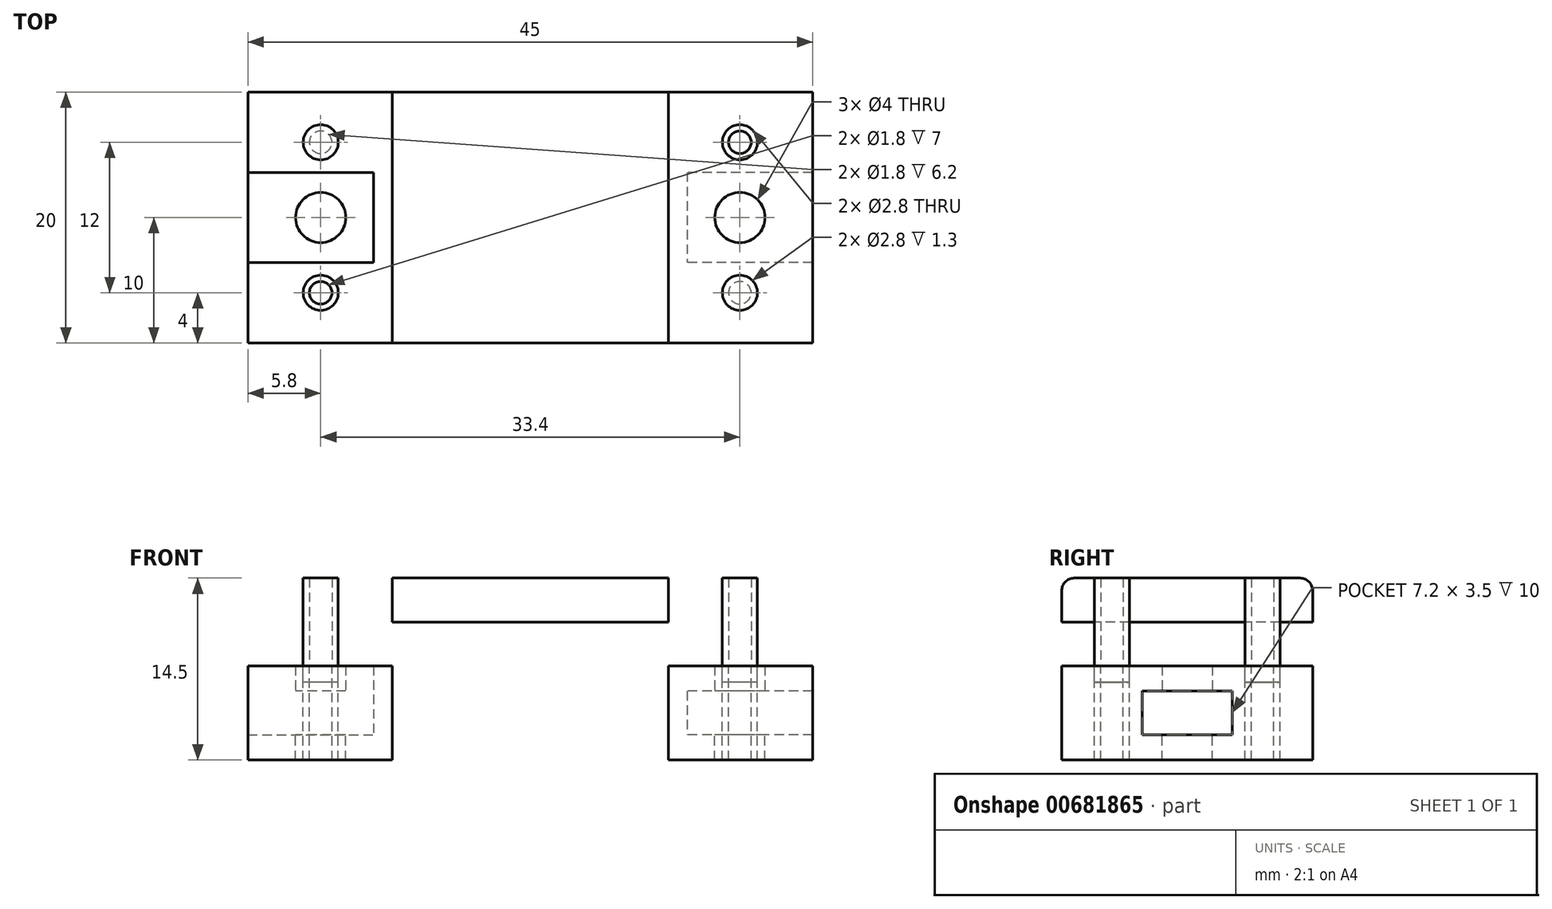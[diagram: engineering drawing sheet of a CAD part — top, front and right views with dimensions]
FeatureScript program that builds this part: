
annotation { "Feature Type Name" : "Feature", "Feature Type Description" : "" }
export const myFeature = defineFeature(function(context is Context, id is Id, definition is map)
    precondition{}
    {
        {
            var Q0;
            Q0=qCreatedBy(makeId("Top.planeOp"),FACE);
            var sketch = newSketch(context, id + "F0", { "sketchPlane" : qUnion([Q0])});
            skLineSegment(sketch, "E0.bottom", {"start": v(22.5, 10) * mm, "end": v(-22.5, 10) * mm});
            skLineSegment(sketch, "E0.top", {"start": v(22.5, -10) * mm, "end": v(-22.5, -10) * mm});
            skLineSegment(sketch, "E0.left", {"start": v(22.5, 10) * mm, "end": v(22.5, -10) * mm});
            skLineSegment(sketch, "E0.right", {"start": v(-22.5, 10) * mm, "end": v(-22.5, -10) * mm});
            skPoint(sketch, "E0.middle", {"position": v(0, 0) * mm});
            skLineSegment(sketch, "E1.bottom", {"start": v(-22.5, 3.6) * mm, "end": v(-12.5, 3.6) * mm});
            skLineSegment(sketch, "E1.top", {"start": v(-22.5, -3.6) * mm, "end": v(-12.5, -3.6) * mm});
            skLineSegment(sketch, "E1.left", {"start": v(-22.5, 3.6) * mm, "end": v(-22.5, -3.6) * mm});
            skLineSegment(sketch, "E1.right", {"start": v(-12.5, 3.6) * mm, "end": v(-12.5, -3.6) * mm});
            skPoint(sketch, "E2", {"position": v(-22.5, 0) * mm});
            skLineSegment(sketch, "E3.MirrorCS", {"start": v(22.5, 3.6) * mm, "end": v(12.5, 3.6) * mm});
            skLineSegment(sketch, "E4.MirrorCS", {"start": v(12.5, 3.6) * mm, "end": v(12.5, -3.6) * mm});
            skLineSegment(sketch, "E5.MirrorCS", {"start": v(22.5, -3.6) * mm, "end": v(12.5, -3.6) * mm});
            skLineSegment(sketch, "E6", {"start": v(12.5, 0) * mm, "end": v(14.7, 0) * mm, "construction": true});
            skCircle(sketch, "E7", {"center": v(16.7, 0) * mm, "radius": 2 * mm});
            skPoint(sketch, "E8", {"position": v(18.7, 0) * mm});
            skPoint(sketch, "E9", {"position": v(14.7, 0) * mm});
            skCircle(sketch, "E10.MirrorC", {"center": v(-16.7, 0) * mm, "radius": 2 * mm});
            skSolve(sketch);
        }
        {
            var Q0;
            {var subQ1=sQuery(id+"F0.wireOp",EDGE,"E0.bottom");Q0=makeQuery(id+"F0.imprint","IMPRINT",FACE,{"disambiguationData":[TD([[makeQuery(id+"F0.imprint","IMPRINT",EDGE,{"derivedFrom":subQ1}),1.0]])]});}
            var Q1;
            Q1=makeQuery(id+"F0.imprint","IMPRINT",FACE,{"disambiguationData":[TD([[makeQuery(id+"F0.imprint","IMPRINT",EDGE,{"derivedFrom":sQuery(id+"F0.wireOp",EDGE,"E1.bottom")}),-1.0]])]});
            var Q2;
            {var subQ0=sQuery(id+"F0.wireOp",EDGE,"E3.MirrorCS");Q2=makeQuery(id+"F0.imprint","IMPRINT",FACE,{"disambiguationData":[TD([[makeQuery(id+"F0.imprint","IMPRINT",EDGE,{"derivedFrom":subQ0}),1.0]])]});}
            extrude(context, id + "F1", {"entities" : qUnion([Q0, Q1, Q2]), "oppositeDirection" : true, "depth" : 2 * mm, "offsetDistance" : 25 * mm});
        }
        {
            var Q0;
            {var subQ5=sQuery(id+"F0.wireOp",EDGE,"E0.bottom");Q0=makeQuery(id+"F0.imprint","IMPRINT",FACE,{"disambiguationData":[TD([[makeQuery(id+"F0.imprint","IMPRINT",EDGE,{"derivedFrom":subQ5}),1.0]])]});}
            extrude(context, id + "F2", {"entities" : qUnion([Q0]), "operationType" : NewBodyOperationType.ADD, "depth" : 3.5 * mm, "offsetDistance" : 25 * mm});
        }
        {
            var Q0;
            Q0=makeQuery(id+"F2.opExtrude","CAP_FACE",FACE,{"disambiguationData":[OSD([sQuery(id+"F0.wireOp",EDGE,"E0.bottom"),sQuery(id+"F0.wireOp",EDGE,"E0.top"),sQuery(id+"F0.wireOp",EDGE,"E0.left"),sQuery(id+"F0.wireOp",EDGE,"E0.right"),sQuery(id+"F0.wireOp",EDGE,"E1.bottom"),sQuery(id+"F0.wireOp",EDGE,"E1.top"),sQuery(id+"F0.wireOp",EDGE,"E1.right"),sQuery(id+"F0.wireOp",EDGE,"E3.MirrorCS"),sQuery(id+"F0.wireOp",EDGE,"E4.MirrorCS"),sQuery(id+"F0.wireOp",EDGE,"E5.MirrorCS")])],"isStart":false});
            var sketch = newSketch(context, id + "F3", { "sketchPlane" : qUnion([Q0])});
            skLineSegment(sketch, "E11.bottom", {"start": v(-22.5, 10) * mm, "end": v(22.5, 10) * mm});
            skLineSegment(sketch, "E11.top", {"start": v(-22.5, -10) * mm, "end": v(22.5, -10) * mm});
            skLineSegment(sketch, "E11.left", {"start": v(-22.5, 10) * mm, "end": v(-22.5, -10) * mm});
            skLineSegment(sketch, "E11.right", {"start": v(22.5, 10) * mm, "end": v(22.5, -10) * mm});
            skSolve(sketch);
        }
        {
            var Q0;
            Q0 = qSketchRegion(id + "F3", true);
            extrude(context, id + "F4", {"entities" : qUnion([Q0]), "operationType" : NewBodyOperationType.ADD, "depth" : 2 * mm, "offsetDistance" : 25 * mm});
        }
        {
            var Q0;
            Q0=makeQuery(id+"F0.imprint","IMPRINT",FACE,{"disambiguationData":[TD([[makeQuery(id+"F0.imprint","IMPRINT",EDGE,{"derivedFrom":sQuery(id+"F0.wireOp",EDGE,"E7")}),1.0]])]});
            var Q1;
            Q1=makeQuery(id+"F0.imprint","IMPRINT",FACE,{"disambiguationData":[TD([[makeQuery(id+"F0.imprint","IMPRINT",EDGE,{"derivedFrom":sQuery(id+"F0.wireOp",EDGE,"E10.MirrorC")}),-1.0]])]});
            extrude(context, id + "F5", {"entities" : qUnion([Q0, Q1]), "operationType" : NewBodyOperationType.REMOVE, "depth" : 25 * mm, "offsetDistance" : 25 * mm});
        }
        {
            var Q0;
            Q0=makeQuery(id+"F4.opExtrude","CAP_FACE",FACE,{"disambiguationData":[OSD([sQuery(id+"F3.wireOp",EDGE,"E11.bottom"),sQuery(id+"F3.wireOp",EDGE,"E11.top"),sQuery(id+"F3.wireOp",EDGE,"E11.left"),sQuery(id+"F3.wireOp",EDGE,"E11.right")])],"isStart":false});
            var sketch = newSketch(context, id + "F6", { "sketchPlane" : qUnion([Q0])});
            skLineSegment(sketch, "E12.bottom", {"start": v(11, 10) * mm, "end": v(-11, 10) * mm});
            skLineSegment(sketch, "E12.top", {"start": v(11, -10) * mm, "end": v(-11, -10) * mm});
            skLineSegment(sketch, "E12.left", {"start": v(11, 10) * mm, "end": v(11, -10) * mm});
            skLineSegment(sketch, "E12.right", {"start": v(-11, 10) * mm, "end": v(-11, -10) * mm});
            skPoint(sketch, "E12.middle", {"position": v(0, 0) * mm});
            skLineSegment(sketch, "E13", {"start": v(-16.7, 10) * mm, "end": v(-16.7, 2) * mm, "construction": true});
            skPoint(sketch, "E14", {"position": v(-16.7, 6) * mm});
            skCircle(sketch, "E15", {"center": v(-16.7, 6) * mm, "radius": 0.9 * mm});
            skCircle(sketch, "E16", {"center": v(-16.7, 6) * mm, "radius": 1.4 * mm});
            skCircle(sketch, "E17.MirrorC", {"center": v(16.7, 6) * mm, "radius": 1.4 * mm});
            skCircle(sketch, "E18.MirrorC", {"center": v(16.7, 6) * mm, "radius": 0.9 * mm});
            skCircle(sketch, "E19.MirrorC", {"center": v(-16.7, -6) * mm, "radius": 1.4 * mm});
            skCircle(sketch, "E20.MirrorC", {"center": v(-16.7, -6) * mm, "radius": 0.9 * mm});
            skCircle(sketch, "E21.MirrorC", {"center": v(16.7, -6) * mm, "radius": 1.4 * mm});
            skCircle(sketch, "E22.MirrorC", {"center": v(16.7, -6) * mm, "radius": 0.9 * mm});
            skSolve(sketch);
        }
        {
            var Q0;
            Q0=makeQuery(id+"F6.imprint","IMPRINT",FACE,{"disambiguationData":[TD([[makeQuery(id+"F6.imprint","IMPRINT",EDGE,{"derivedFrom":sQuery(id+"F6.wireOp",EDGE,"E12.bottom")}),1.0]])]});
            var Q1;
            Q1=makeQuery(id+"F6.imprint","IMPRINT",FACE,{"disambiguationData":[TD([[makeQuery(id+"F6.imprint","IMPRINT",EDGE,{"derivedFrom":sQuery(id+"F6.wireOp",EDGE,"E15")}),1.0]])]});
            var Q2;
            Q2=makeQuery(id+"F6.imprint","IMPRINT",FACE,{"disambiguationData":[TD([[makeQuery(id+"F6.imprint","IMPRINT",EDGE,{"derivedFrom":sQuery(id+"F6.wireOp",EDGE,"E18.MirrorC")}),-1.0]])]});
            var Q3;
            Q3=makeQuery(id+"F6.imprint","IMPRINT",FACE,{"disambiguationData":[TD([[makeQuery(id+"F6.imprint","IMPRINT",EDGE,{"derivedFrom":sQuery(id+"F6.wireOp",EDGE,"E22.MirrorC")}),1.0]])]});
            var Q4;
            Q4=makeQuery(id+"F6.imprint","IMPRINT",FACE,{"disambiguationData":[TD([[makeQuery(id+"F6.imprint","IMPRINT",EDGE,{"derivedFrom":sQuery(id+"F6.wireOp",EDGE,"E20.MirrorC")}),-1.0]])]});
            var Q5;
            {var subQ0=sQuery(id+"F0.wireOp",EDGE,"E0.right");var subQ1=sQuery(id+"F0.wireOp",EDGE,"E0.top");var subQ2=sQuery(id+"F0.wireOp",EDGE,"E1.left");var subQ4=sQuery(id+"F0.wireOp",EDGE,"E0.bottom");var subQ6=sQuery(id+"F0.wireOp",EDGE,"E10.MirrorC");Q5=makeQuery(id+"F2.boolean.opBoolean","SPLIT",FACE,{"disambiguationData":[TD([makeQuery(id+"F1.opExtrude","SWEPT_FACE",FACE,{"disambiguationData":[OSD([subQ6])]})])],"derivedFrom":makeQuery(id+"F1.opExtrude","CAP_FACE",FACE,{"disambiguationData":[OSD([subQ4,subQ1,sQuery(id+"F0.wireOp",EDGE,"E0.left"),subQ0,subQ2,sQuery(id+"F0.wireOp",EDGE,"E7"),subQ6])],"isStart":true})});}
            extrude(context, id + "F7", {"entities" : qUnion([Q0, Q1, Q2, Q3, Q4]), "operationType" : NewBodyOperationType.REMOVE, "oppositeDirection" : true, "depth" : 25 * mm, "endBoundEntityFace" : qUnion([Q5]), "offsetDistance" : 25 * mm});
        }
        {
            var Q0;
            Q0=makeQuery(id+"F6.imprint","IMPRINT",FACE,{"disambiguationData":[TD([[makeQuery(id+"F6.imprint","IMPRINT",EDGE,{"derivedFrom":sQuery(id+"F6.wireOp",EDGE,"E15")}),-1.0]])]});
            var Q1;
            Q1=makeQuery(id+"F6.imprint","IMPRINT",FACE,{"disambiguationData":[TD([[makeQuery(id+"F6.imprint","IMPRINT",EDGE,{"derivedFrom":sQuery(id+"F6.wireOp",EDGE,"E19.MirrorC")}),-1.0]])]});
            var Q2;
            Q2=makeQuery(id+"F6.imprint","IMPRINT",FACE,{"disambiguationData":[TD([[makeQuery(id+"F6.imprint","IMPRINT",EDGE,{"derivedFrom":sQuery(id+"F6.wireOp",EDGE,"E21.MirrorC")}),1.0]])]});
            var Q3;
            Q3=makeQuery(id+"F6.imprint","IMPRINT",FACE,{"disambiguationData":[TD([[makeQuery(id+"F6.imprint","IMPRINT",EDGE,{"derivedFrom":sQuery(id+"F6.wireOp",EDGE,"E17.MirrorC")}),-1.0]])]});
            extrude(context, id + "F8", {"entities" : qUnion([Q0, Q1, Q2, Q3]), "operationType" : NewBodyOperationType.REMOVE, "oppositeDirection" : true, "depth" : 1.3 * mm, "offsetDistance" : 25 * mm});
        }
        {
            var Q0;
            {var subQ4=sQuery(id+"F6.wireOp",EDGE,"E12.right");Q0=makeQuery(id+"F6.imprint","IMPRINT",FACE,{"disambiguationData":[TD([[makeQuery(id+"F6.imprint","IMPRINT",EDGE,{"derivedFrom":subQ4}),-1.0]])]});}
            var Q1;
            Q1=makeQuery(id+"F6.imprint","IMPRINT",FACE,{"disambiguationData":[TD([[makeQuery(id+"F6.imprint","IMPRINT",EDGE,{"derivedFrom":sQuery(id+"F6.wireOp",EDGE,"E12.bottom")}),1.0]])]});
            var Q2;
            {var subQ2=sQuery(id+"F6.wireOp",EDGE,"E12.left");Q2=makeQuery(id+"F6.imprint","IMPRINT",FACE,{"disambiguationData":[TD([[makeQuery(id+"F6.imprint","IMPRINT",EDGE,{"derivedFrom":subQ2}),1.0]])]});}
            var Q3;
            Q3=makeQuery(id+"F6.imprint","IMPRINT",FACE,{"disambiguationData":[TD([[makeQuery(id+"F6.imprint","IMPRINT",EDGE,{"derivedFrom":sQuery(id+"F6.wireOp",EDGE,"E17.MirrorC")}),-1.0]])]});
            var Q4;
            Q4=makeQuery(id+"F6.imprint","IMPRINT",FACE,{"disambiguationData":[TD([[makeQuery(id+"F6.imprint","IMPRINT",EDGE,{"derivedFrom":sQuery(id+"F6.wireOp",EDGE,"E18.MirrorC")}),-1.0]])]});
            var Q5;
            Q5=makeQuery(id+"F6.imprint","IMPRINT",FACE,{"disambiguationData":[TD([[makeQuery(id+"F6.imprint","IMPRINT",EDGE,{"derivedFrom":sQuery(id+"F6.wireOp",EDGE,"E21.MirrorC")}),1.0]])]});
            var Q6;
            Q6=makeQuery(id+"F6.imprint","IMPRINT",FACE,{"disambiguationData":[TD([[makeQuery(id+"F6.imprint","IMPRINT",EDGE,{"derivedFrom":sQuery(id+"F6.wireOp",EDGE,"E22.MirrorC")}),1.0]])]});
            var Q7;
            Q7=makeQuery(id+"F6.imprint","IMPRINT",FACE,{"disambiguationData":[TD([[makeQuery(id+"F6.imprint","IMPRINT",EDGE,{"derivedFrom":sQuery(id+"F6.wireOp",EDGE,"E20.MirrorC")}),-1.0]])]});
            var Q8;
            Q8=makeQuery(id+"F6.imprint","IMPRINT",FACE,{"disambiguationData":[TD([[makeQuery(id+"F6.imprint","IMPRINT",EDGE,{"derivedFrom":sQuery(id+"F6.wireOp",EDGE,"E19.MirrorC")}),-1.0]])]});
            var Q9;
            Q9=makeQuery(id+"F6.imprint","IMPRINT",FACE,{"disambiguationData":[TD([[makeQuery(id+"F6.imprint","IMPRINT",EDGE,{"derivedFrom":sQuery(id+"F6.wireOp",EDGE,"E15")}),-1.0]])]});
            var Q10;
            Q10=makeQuery(id+"F6.imprint","IMPRINT",FACE,{"disambiguationData":[TD([[makeQuery(id+"F6.imprint","IMPRINT",EDGE,{"derivedFrom":sQuery(id+"F6.wireOp",EDGE,"E15")}),1.0]])]});
            extrude(context, id + "F9", {"entities" : qUnion([Q0, Q1, Q2, Q3, Q4, Q5, Q6, Q7, Q8, Q9, Q10]), "depth" : 7 * mm, "offsetDistance" : 25 * mm});
        }
        {
            var Q0;
            Q0=makeQuery(id+"F9.opExtrude","CAP_FACE",FACE,{"disambiguationData":[OSD([sQuery(id+"F0.wireOp",EDGE,"E7"),sQuery(id+"F0.wireOp",EDGE,"E10.MirrorC"),sQuery(id+"F3.wireOp",EDGE,"E11.bottom"),sQuery(id+"F3.wireOp",EDGE,"E11.top"),sQuery(id+"F3.wireOp",EDGE,"E11.left"),sQuery(id+"F3.wireOp",EDGE,"E11.right"),sQuery(id+"F6.wireOp",EDGE,"E12.bottom"),sQuery(id+"F6.wireOp",EDGE,"E12.top")])],"isStart":false});
            var sketch = newSketch(context, id + "F10", { "sketchPlane" : qUnion([Q0])});
            skCircle(sketch, "E23.0", {"center": v(-16.7, 0) * mm, "radius": 3.6 * mm});
            skLineSegment(sketch, "E24", {"start": v(-16.7, 2) * mm, "end": v(-16.7, -2) * mm, "construction": true});
            skCircle(sketch, "E25.MirrorC", {"center": v(16.7, 0) * mm, "radius": 3.6 * mm});
            skSolve(sketch);
        }
        {
            var Q0;
            Q0=makeQuery(id+"F10.imprint","IMPRINT",FACE,{"disambiguationData":[TD([[makeQuery(id+"F10.imprint","IMPRINT",EDGE,{"derivedFrom":sQuery(id+"F10.wireOp",EDGE,"E23.0")}),1.0]])]});
            var Q1;
            Q1=makeQuery(id+"F10.imprint","IMPRINT",FACE,{"disambiguationData":[TD([[makeQuery(id+"F10.imprint","IMPRINT",EDGE,{"derivedFrom":sQuery(id+"F10.wireOp",EDGE,"E25.MirrorC")}),-1.0]])]});
            extrude(context, id + "F11", {"entities" : qUnion([Q0, Q1]), "operationType" : NewBodyOperationType.REMOVE, "oppositeDirection" : true, "depth" : 2.5 * mm, "offsetDistance" : 25 * mm});
        }
        {
            var Q0;
            Q0=makeQuery(id+"F9.opExtrude","CAP_EDGE",EDGE,{"disambiguationData":[OSD([sQuery(id+"F3.wireOp",EDGE,"E11.top"),sQuery(id+"F6.wireOp",EDGE,"E12.top")])],"isStart":false});
            var Q1;
            Q1=makeQuery(id+"F9.opExtrude","CAP_EDGE",EDGE,{"disambiguationData":[OSD([sQuery(id+"F3.wireOp",EDGE,"E11.right")])],"isStart":false});
            var Q2;
            Q2=makeQuery(id+"F9.opExtrude","CAP_EDGE",EDGE,{"disambiguationData":[OSD([sQuery(id+"F3.wireOp",EDGE,"E11.bottom"),sQuery(id+"F6.wireOp",EDGE,"E12.bottom")])],"isStart":false});
            var Q3;
            Q3=makeQuery(id+"F9.opExtrude","CAP_EDGE",EDGE,{"disambiguationData":[OSD([sQuery(id+"F3.wireOp",EDGE,"E11.left")])],"isStart":false});
            fillet(context, id + "F12", {"entities" : qUnion([Q0, Q1, Q2, Q3]), "radius" : 1 * mm, "tangentPropagation" : true, "allowEdgeOverflow" : false});
        }
        {
            var Q0;
            Q0=makeQuery(id+"F9.opExtrude","SWEPT_FACE",FACE,{"disambiguationData":[OSD([sQuery(id+"F3.wireOp",EDGE,"E11.top"),sQuery(id+"F6.wireOp",EDGE,"E12.top")])]});
            var sketch = newSketch(context, id + "F13", { "sketchPlane" : qUnion([Q0])});
            skLineSegment(sketch, "E26", {"start": v(-22.5, 5.5) * mm, "end": v(-11, 5.5) * mm, "construction": true});
            skLineSegment(sketch, "E27", {"start": v(22.5, 5.5) * mm, "end": v(11, 5.5) * mm, "construction": true});
            skLineSegment(sketch, "E28.bottom", {"start": v(-11, 5.5) * mm, "end": v(11, 5.5) * mm});
            skLineSegment(sketch, "E28.top", {"start": v(-11, 9) * mm, "end": v(11, 9) * mm});
            skLineSegment(sketch, "E28.left", {"start": v(-11, 5.5) * mm, "end": v(-11, 9) * mm});
            skLineSegment(sketch, "E28.right", {"start": v(11, 5.5) * mm, "end": v(11, 9) * mm});
            skSolve(sketch);
        }
        {
            var Q0;
            Q0=makeQuery(id+"F13.imprint","IMPRINT",FACE,{"disambiguationData":[TD([[makeQuery(id+"F13.imprint","IMPRINT",EDGE,{"derivedFrom":sQuery(id+"F13.wireOp",EDGE,"E28.bottom")}),-1.0]])]});
            extrude(context, id + "F14", {"entities" : qUnion([Q0]), "operationType" : NewBodyOperationType.REMOVE, "oppositeDirection" : true, "depth" : 25 * mm, "offsetDistance" : 25 * mm});
        }
    });
